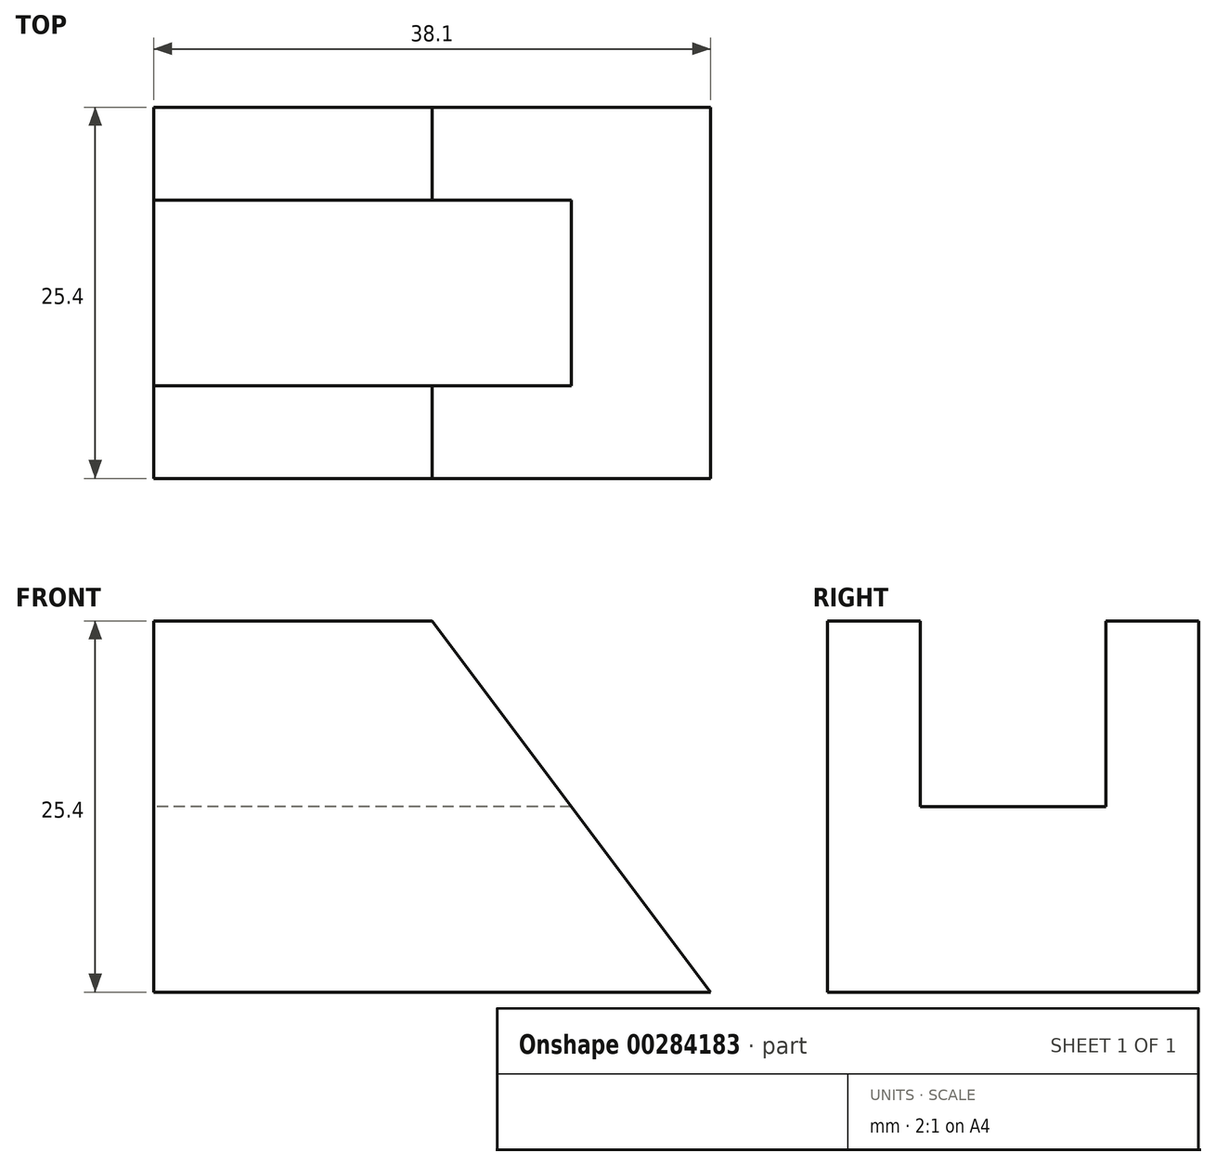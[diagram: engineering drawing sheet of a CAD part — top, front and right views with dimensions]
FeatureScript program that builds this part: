
annotation { "Feature Type Name" : "Feature", "Feature Type Description" : "" }
export const myFeature = defineFeature(function(context is Context, id is Id, definition is map)
    precondition{}
    {
        {
            var Q0;
            Q0=qCreatedBy(makeId("Front.planeOp"),FACE);
            var sketch = newSketch(context, id + "F0", { "sketchPlane" : qUnion([Q0])});
            skLineSegment(sketch, "E0", {"start": v(0, 0) * mm, "end": v(38.1, 0) * mm});
            skLineSegment(sketch, "E1", {"start": v(38.1, 0) * mm, "end": v(19.05, 25.4) * mm});
            skLineSegment(sketch, "E2", {"start": v(19.05, 25.4) * mm, "end": v(0, 25.4) * mm});
            skLineSegment(sketch, "E3", {"start": v(0, 25.4) * mm, "end": v(0, 0) * mm});
            skSolve(sketch);
        }
        {
            var Q0;
            Q0 = qSketchRegion(id + "F0", true);
            extrude(context, id + "F1", {"entities" : qUnion([Q0]), "depth" : 25.4 * mm, "symmetric" : true});
        }
        {
            var Q0;
            Q0=makeQuery(id+"F1.opExtrude","SWEPT_FACE",FACE,{"disambiguationData":[OSD([sQuery(id+"F0.wireOp",EDGE,"E3")])]});
            var sketch = newSketch(context, id + "F2", { "sketchPlane" : qUnion([Q0])});
            skLineSegment(sketch, "E4", {"start": v(-12.7, -9.96) * mm, "end": v(-6.35, -9.96) * mm});
            skLineSegment(sketch, "E5", {"start": v(-6.35, 25.4) * mm, "end": v(-6.35, 12.7) * mm});
            skLineSegment(sketch, "E6", {"start": v(-6.35, 12.7) * mm, "end": v(6.35, 12.7) * mm});
            skLineSegment(sketch, "E7", {"start": v(6.35, 12.7) * mm, "end": v(6.35, 25.4) * mm});
            skLineSegment(sketch, "E8", {"start": v(6.35, 25.4) * mm, "end": v(-6.35, 25.4) * mm});
            skSolve(sketch);
        }
        {
            var Q0;
            Q0=makeQuery(id+"F2.imprint","IMPRINT",FACE,{"disambiguationData":[TD([[makeQuery(id+"F2.imprint","IMPRINT",EDGE,{"derivedFrom":sQuery(id+"F2.wireOp",EDGE,"E5")}),1.0]])]});
            extrude(context, id + "F3", {"entities" : qUnion([Q0]), "operationType" : NewBodyOperationType.REMOVE, "endBound" : BoundingType.THROUGH_ALL, "oppositeDirection" : true, "depth" : 25.4 * mm});
        }
    });
